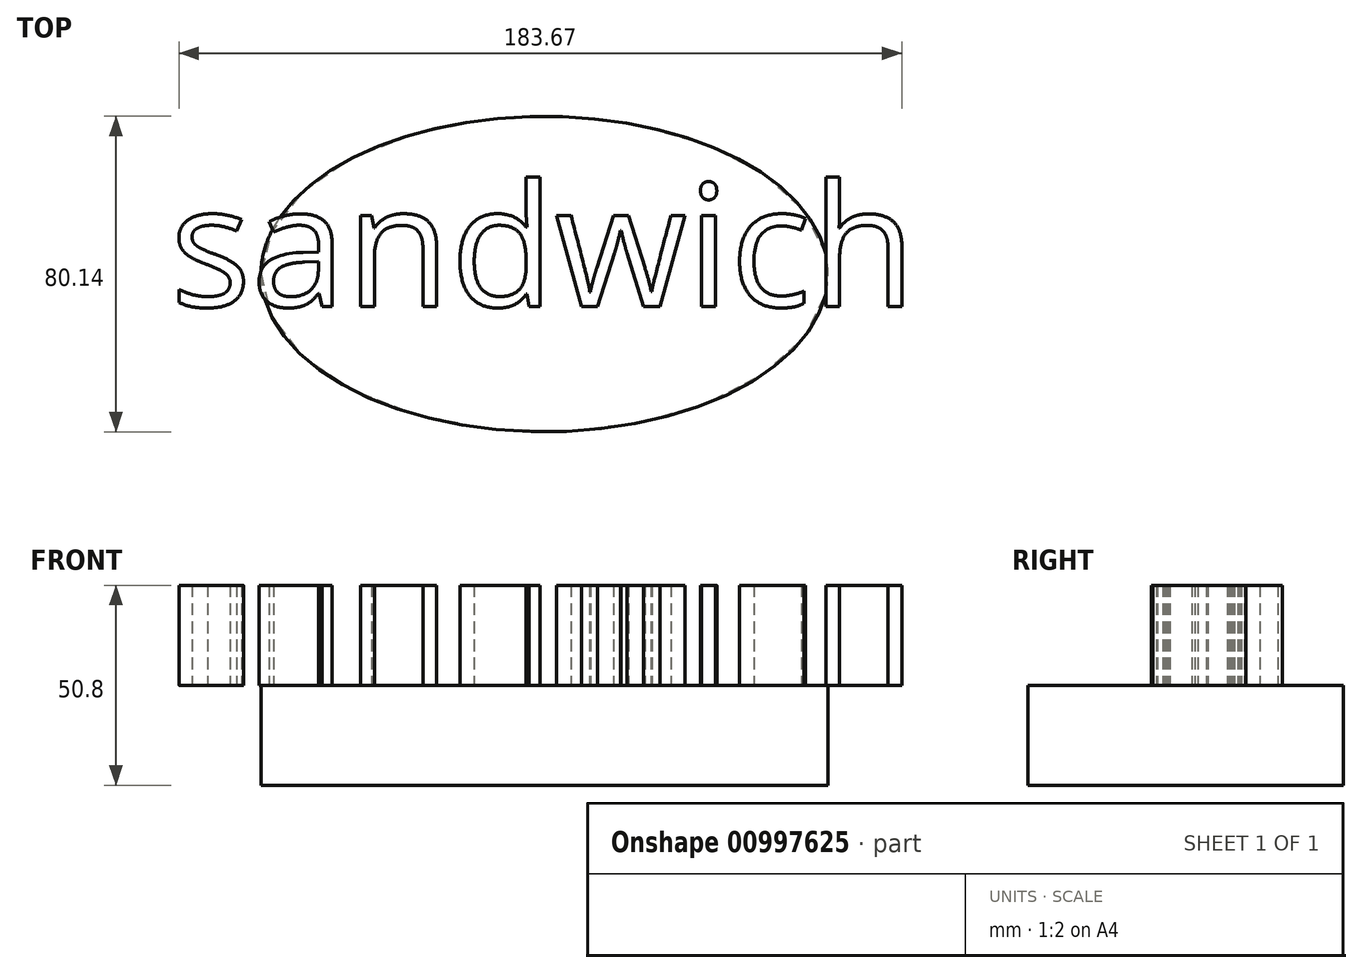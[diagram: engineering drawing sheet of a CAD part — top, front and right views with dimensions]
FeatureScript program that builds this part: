
annotation { "Feature Type Name" : "Feature", "Feature Type Description" : "" }
export const myFeature = defineFeature(function(context is Context, id is Id, definition is map)
    precondition{}
    {
        {
            var Q0;
            Q0=qCreatedBy(makeId("Top.planeOp"),FACE);
            var sketch = newSketch(context, id + "F0", { "sketchPlane" : qUnion([Q0])});
            skEllipse(sketch, "E0", {"center": v(0, 0) * mm, "majorRadius": 72.03 * mm, "minorRadius": 40.07 * mm, "majorAxis": v(-1, 0)});
            skSolve(sketch);
        }
        {
            var Q0;
            Q0=makeQuery(id+"F0.imprint","IMPRINT",FACE,{"disambiguationData":[TD([[makeQuery(id+"F0.imprint","IMPRINT",EDGE,{"derivedFrom":sQuery(id+"F0.wireOp",EDGE,"E0")}),1.0]])]});
            extrude(context, id + "F1", {"entities" : qUnion([Q0]), "depth" : 25.4 * mm, "offsetDistance" : 25.4 * mm});
        }
        {
            var Q0;
            Q0=makeQuery(id+"F1.opExtrude","CAP_FACE",FACE,{"disambiguationData":[OSD([sQuery(id+"F0.wireOp",EDGE,"E0")])],"isStart":false});
            var sketch = newSketch(context, id + "F2", { "sketchPlane" : qUnion([Q0])});
            skText(sketch, "E1", { "text": "sandwich", "fontName": "OpenSans-Regular.ttf"});
            const initialGuessF2  = {"E1": [-0.09511, -0.00823, 1, 0, 0.03113]};
            skSetInitialGuess(sketch, initialGuessF2);
            skSolve(sketch);
        }
        {
            var Q0;
            Q0 = qSketchRegion(id + "F2", true);
            extrude(context, id + "F3", {"entities" : qUnion([Q0]), "operationType" : NewBodyOperationType.ADD, "depth" : 25.4 * mm, "offsetDistance" : 25.4 * mm});
        }
    });
